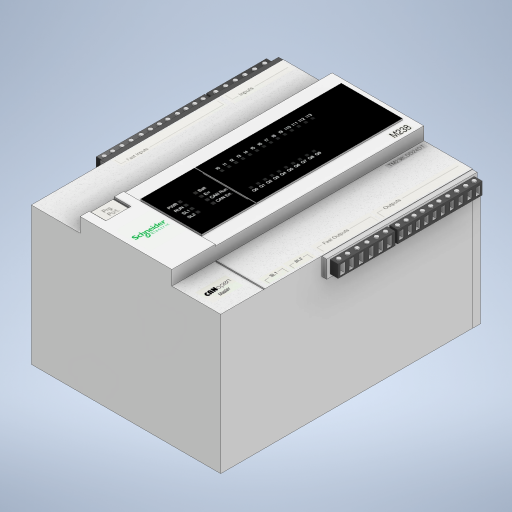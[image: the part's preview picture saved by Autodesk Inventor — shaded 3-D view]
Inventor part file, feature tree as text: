
AUTODESK INVENTOR PART (.ipt)
format: ipt  version: 2023 (Build 270158000, 158)  size: 1,148,416 bytes
history: native  units: in
note: dims shown in document units (in); Inventor stores cm internally (conversion verified against a paired STEP export)
features: extrude x85, sketch x29, other x26
ambient origin geometry x8: Origin, YZ Plane, XZ Plane, XY Plane, X Axis, Y Axis, Z Axis, Center Point
bodies: Solid1 (feature_tree)
feature tree (140):
  extrude  "Extrusion1"  Depth=0.315in TaperAngle=0.0deg
  extrude  "Extrusion2"  Depth=0.0394in TaperAngle=0.0deg
  sketch  "Sketch3"  dims[d10=0.0394in d11=0.0in d12=0.0394in d13=0.0in]
  extrude  "Extrusion3"  Depth=0.0394in TaperAngle=0.0deg
  extrude  "Extrusion4"  Depth=0.1969in TaperAngle=0.0deg
  extrude  "Extrusion5"  Depth=0.1in
  extrude  "Extrusion6"  Depth=0.1in
  extrude  "Extrusion7"  Depth=0.1in
  sketch  "Sketch6"  dims[d21=0.1in d22=0.1in d23=0.1in]
  extrude  "Extrusion8"  Depth=0.0197in TaperAngle=0.0deg
  extrude  "Extrusion9"  Depth=0.0197in TaperAngle=0.0deg
  sketch  "Sketch7"  dims[d24=0.1in d25=0.1in d26=0.1in d27=0.1in d28=0.1in d29=0.1in d30=0.1in d31=0.1in]
  extrude  "Extrusion10"  Depth=0.0197in TaperAngle=0.0deg
  extrude  "Extrusion11"  Depth=0.0197in TaperAngle=0.0deg
  extrude  "Extrusion12"  Depth=0.0197in TaperAngle=0.0deg
  extrude  "Extrusion13"  Depth=0.0197in TaperAngle=0.0deg
  extrude  "Extrusion14"  Depth=0.1in
  extrude  "Extrusion15"  Depth=0.1in
  extrude  "Extrusion16"  Depth=0.0197in TaperAngle=0.0deg
  extrude  "Extrusion17"  Depth=0.0197in TaperAngle=0.0deg
  extrude  "Extrusion18"  Depth=0.0197in TaperAngle=0.0deg
  extrude  "Extrusion19"  Depth=0.1181in TaperAngle=0.0deg
  extrude  "Extrusion20"  Depth=0.1969in TaperAngle=0.0deg
  extrude  "Extrusion21"  Depth=0.1in
  sketch  "Sketch8"  dims[d32=0.0197in d33=0.0in d34=0.0197in d35=0.0in]
  extrude  "Extrusion22"  Depth=0.1in
  extrude  "Extrusion23"  Depth=0.0197in TaperAngle=0.0deg
  extrude  "Extrusion24"  Depth=0.0197in TaperAngle=0.0deg
  extrude  "Extrusion25"  Depth=0.0197in TaperAngle=0.0deg
  extrude  "Extrusion26"  Depth=0.1in
  extrude  "Extrusion27"  Depth=0.1in
  other  "Decal1"
  sketch  "Sketch10"  dims[d40=0.0197in d41=0.0in d42=0.0197in d43=0.0in]
  other  "Decal2"
  other  "Decal3"
  other  "Decal4"
  other  "Decal5"
  other  "Decal6"
  extrude  "Extrusion28"  Depth=0.0197in TaperAngle=0.0deg
  sketch  "Sketch14"  dims[d56=0.1in d57=0.1in]
  extrude  "Extrusion29"  Depth=0.0197in TaperAngle=0.0deg
  extrude  "Extrusion30"  Depth=0.0197in TaperAngle=0.0deg
  sketch  "Sketch15"  dims[d58=0.1in d59=0.1in d60=0.1in d61=0.1in]
  extrude  "Extrusion31"  Depth=0.0197in TaperAngle=0.0deg
  extrude  "Extrusion32"  Depth=0.0197in TaperAngle=0.0deg
  extrude  "Extrusion33"  Depth=0.0197in TaperAngle=0.0deg
  extrude  "Extrusion34"  Depth=0.0197in TaperAngle=0.0deg
  extrude  "Extrusion35"  Depth=0.0197in TaperAngle=0.0deg
  extrude  "Extrusion36"  Depth=0.0197in TaperAngle=0.0deg
  sketch  "Sketch16"  dims[d62=0.0197in d63=0.0in d64=0.0197in d65=0.0in]
  extrude  "Extrusion37"  Depth=0.1969in TaperAngle=0.0deg
  extrude  "Extrusion38"  Depth=0.1575in TaperAngle=0.0deg
  extrude  "Extrusion39"  Depth=0.1575in TaperAngle=0.0deg
  extrude  "Extrusion40"  Depth=0.1575in TaperAngle=0.0deg
  extrude  "Extrusion41"  Depth=0.1575in TaperAngle=0.0deg
  extrude  "Extrusion42"  Depth=0.1575in TaperAngle=0.0deg
  extrude  "Extrusion43"  Depth=0.1575in TaperAngle=0.0deg
  extrude  "Extrusion44"  Depth=0.1575in TaperAngle=0.0deg
  extrude  "Extrusion45"  Depth=0.1575in TaperAngle=0.0deg
  extrude  "Extrusion46"  Depth=0.1575in TaperAngle=0.0deg
  sketch  "Sketch17"  dims[d66=0.0197in d67=0.0in d68=0.0197in d69=0.0in]
  other  "Decal7"
  other  "Decal8"
  other  "Decal9"
  extrude  "Extrusion47"  Depth=0.1575in TaperAngle=0.0deg
  sketch  "Sketch20"  dims[d274=0.1969in d275=0.0in d276=0.1969in d277=0.0in]
  extrude  "Extrusion48"  Depth=0.1575in TaperAngle=0.0deg
  extrude  "Extrusion49"  Depth=0.1575in TaperAngle=0.0deg
  extrude  "Extrusion50"  Depth=0.1575in TaperAngle=0.0deg
  extrude  "Extrusion51"  Depth=0.1575in TaperAngle=0.0deg
  extrude  "Extrusion52"  Depth=0.1575in TaperAngle=0.0deg
  extrude  "Extrusion53"  Depth=0.1575in TaperAngle=0.0deg
  extrude  "Extrusion54"  Depth=0.1575in TaperAngle=0.0deg
  extrude  "Extrusion55"  Depth=0.1575in TaperAngle=0.0deg
  extrude  "Extrusion56"  Depth=0.1575in TaperAngle=0.0deg
  extrude  "Extrusion57"  Depth=0.1575in TaperAngle=0.0deg
  extrude  "Extrusion58"  Depth=0.1575in TaperAngle=0.0deg
  extrude  "Extrusion59"  Depth=0.1575in TaperAngle=0.0deg
  extrude  "Extrusion60"  Depth=0.1575in TaperAngle=0.0deg
  sketch  "Sketch21"  dims[d278=0.1in d279=0.1in]
  extrude  "Extrusion61"  Depth=0.1575in TaperAngle=0.0deg
  extrude  "Extrusion62"  Depth=0.1575in TaperAngle=0.0deg
  extrude  "Extrusion63"  Depth=0.1575in TaperAngle=0.0deg
  extrude  "Extrusion64"  Depth=0.1575in TaperAngle=0.0deg
  extrude  "Extrusion65"  Depth=0.1575in TaperAngle=0.0deg
  extrude  "Extrusion66"  Depth=0.1575in TaperAngle=0.0deg
  sketch  "Sketch22"  dims[d280=0.1in d281=0.1in d282=0.1in d283=0.1in]
  extrude  "Extrusion67"  Depth=0.1575in TaperAngle=0.0deg
  extrude  "Extrusion68"  Depth=0.1575in TaperAngle=0.0deg
  extrude  "Extrusion69"  Depth=0.1575in TaperAngle=0.0deg
  extrude  "Extrusion70"  Depth=0.1575in TaperAngle=0.0deg
  extrude  "Extrusion71"  Depth=0.1575in TaperAngle=0.0deg
  extrude  "Extrusion72"  Depth=0.1575in TaperAngle=0.0deg
  sketch  "Sketch23"  dims[d284=0.0197in d285=0.0in d286=0.0197in d287=0.0in]
  extrude  "Extrusion73"  Depth=0.1575in TaperAngle=0.0deg
  extrude  "Extrusion74"  Depth=0.0787in TaperAngle=0.0deg
  extrude  "Extrusion75"  Depth=0.3937in TaperAngle=0.0deg
  extrude  "Extrusion76"  [1 undecoded]
  extrude  "Extrusion77"  [1 undecoded]
  extrude  "Extrusion78"  [1 undecoded]
  extrude  "Extrusion79"  [1 undecoded]
  extrude  "Extrusion80"  [1 undecoded]
  extrude  "Extrusion81"  [1 undecoded]
  extrude  "Extrusion82"  [1 undecoded]
  extrude  "Extrusion83"  [1 undecoded]
  other  "Decal10"
  sketch  "Sketch25"  dims[d292=0.0197in d293=0.0in d294=0.0197in d295=0.0in]
  other  "Decal11"
  sketch  "Sketch27"  dims[d298=0.1in d299=0.1in d300=0.1in d301=0.1in d302=0.1in d303=0.1in]
  other  "Decal12"
  other  "Decal13"
  extrude  "Extrusion84"  [1 undecoded]
  extrude  "Extrusion85"  [1 undecoded]
  sketch  "Sketch1"  dims[d2=3.3858in d3=0.0in d4=0.315in d5=0.0in]
  sketch  "Sketch2"  dims[d6=0.0394in d7=0.0in d8=0.0394in d9=0.0in]
  sketch  "Sketch4"  dims[d14=0.1181in d15=0.0in d16=0.1969in d17=0.0in]
  sketch  "Sketch5"  dims[d18=0.1969in d19=0.0in d20=0.1in]
  sketch  "Sketch9"  dims[d36=0.0197in d37=0.0in d38=0.0197in d39=0.0in]
  other  "Image4"
  other  "Image5"
  other  "Image7"
  other  "Image9"
  sketch  "Sketch11"  dims[d44=0.0197in d45=0.0in d46=0.0197in d47=0.0in]
  other  "Image12"
  sketch  "Sketch12"  dims[d48=0.0197in d49=0.0in d50=0.0197in d51=0.0in]
  other  "Image13"
  sketch  "Sketch13"  dims[d52=0.0197in d53=0.0in d54=0.0197in d55=0.0in]
  other  "Image14"
  other  "Image15"
  sketch  "Sketch18"  dims[d70=0.0197in d71=0.0in d72=0.0197in d73=0.0in]
  other  "Image16"
  sketch  "Sketch19"  dims[d270=0.4295in d272=0.1181in d273=0.0in]
  sketch  "Sketch24"  dims[d288=0.0197in d289=0.0in d290=0.0197in d291=0.0in]
  other  "Image17"
  sketch  "Sketch26"  dims[d296=0.1in d297=0.1in]
  other  "Image18"
  other  "Image19"
  other  "Image20"
  sketch  "Sketch28"  dims[d304=0.1in d305=0.1in d306=0.0197in d307=0.0in]
  sketch  "Sketch29"  dims[d308=0.0197in d309=0.0in d310=0.0197in d311=0.0in d312=0.0197in d313=0.0in d314=0.0197in d315=0.0in d316=0.0197in d317=0.0in d318=0.0197in d319=0.0in d320=0.0197in d321=0.0in d322=0.0197in d323=0.0in d324=0.0197in d325=0.0in d375=0.1969in d376=0.0in d377=0.1575in d378=0.0in d379=0.1575in d380=0.0in d381=0.1575in d382=0.0in d383=0.1575in d384=0.0in d385=0.1575in d386=0.0in d387=0.1575in d388=0.0in d389=0.1575in d390=0.0in d391=0.1575in d392=0.0in d393=0.1575in d394=0.0in d395=0.1575in d396=0.0in d397=0.1575in d398=0.0in d399=0.1575in d400=0.0in d401=0.1575in d402=0.0in d403=0.1575in d404=0.0in d405=0.1575in d406=0.0in d407=0.1575in d408=0.0in d409=0.1575in d410=0.0in d411=0.1575in d412=0.0in d413=0.1575in d414=0.0in d415=0.1575in d416=0.0in d417=0.1575in d418=0.0in d419=0.1575in d420=0.0in d421=0.1575in d422=0.0in d423=0.1575in d424=0.0in d425=0.1575in d426=0.0in d427=0.1575in d428=0.0in d429=0.1575in d430=0.0in d431=0.1575in d432=0.0in d433=0.1575in d434=0.0in d435=0.1575in d436=0.0in d437=0.1575in d438=0.0in d439=0.1575in d440=0.0in d441=0.1575in d442=0.0in d443=0.1575in d444=0.0in d445=0.1575in d446=0.0in d447=0.1575in d448=0.0in d523=0.0787in d524=0.0in d525=0.3937in d526=0.0in]
note: 10 required parameter values undecoded (feature->parameter linkage not recoverable at this tier; creation-order binding heuristic only, values carry confidence <= 0.55)
